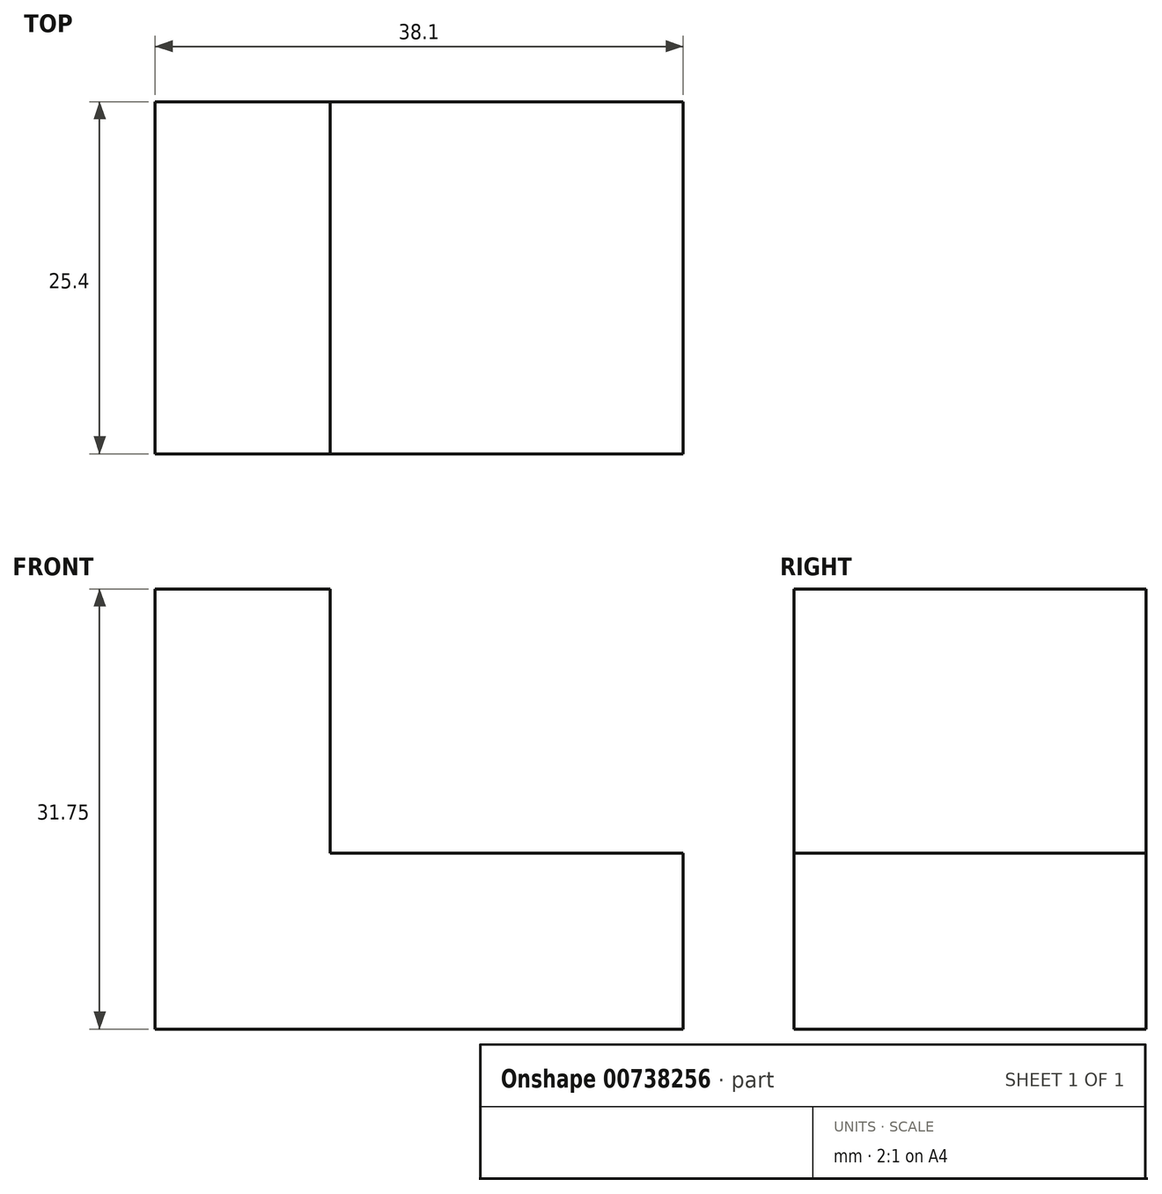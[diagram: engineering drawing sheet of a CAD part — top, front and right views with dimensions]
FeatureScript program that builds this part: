
annotation { "Feature Type Name" : "Feature", "Feature Type Description" : "" }
export const myFeature = defineFeature(function(context is Context, id is Id, definition is map)
    precondition{}
    {
        {
            var Q0;
            Q0=qCreatedBy(makeId("Front.planeOp"),FACE);
            var sketch = newSketch(context, id + "F0", { "sketchPlane" : qUnion([Q0])});
            skLineSegment(sketch, "E0", {"start": v(0, 0) * mm, "end": v(38.1, 0) * mm});
            skLineSegment(sketch, "E1", {"start": v(38.1, 0) * mm, "end": v(38.1, 31.75) * mm});
            skLineSegment(sketch, "E2", {"start": v(38.1, 31.75) * mm, "end": v(0, 31.75) * mm});
            skLineSegment(sketch, "E3", {"start": v(0, 31.75) * mm, "end": v(0, 0) * mm});
            skSolve(sketch);
        }
        {
            var Q0;
            Q0 = qSketchRegion(id + "F0", true);
            extrude(context, id + "F1", {"entities" : qUnion([Q0]), "depth" : 25.4 * mm, "offsetDistance" : 25.4 * mm});
        }
        {
            var Q0;
            Q0=makeQuery(id+"F1.opExtrude","CAP_FACE",FACE,{"disambiguationData":[OSD([sQuery(id+"F0.wireOp",EDGE,"E0"),sQuery(id+"F0.wireOp",EDGE,"E1"),sQuery(id+"F0.wireOp",EDGE,"E2"),sQuery(id+"F0.wireOp",EDGE,"E3")])],"isStart":false});
            var sketch = newSketch(context, id + "F2", { "sketchPlane" : qUnion([Q0])});
            skLineSegment(sketch, "E4", {"start": v(0, 31.75) * mm, "end": v(12.63, 31.75) * mm});
            skLineSegment(sketch, "E5", {"start": v(0, 0) * mm, "end": v(12.63, 0) * mm});
            skLineSegment(sketch, "E6", {"start": v(12.63, 12.7) * mm, "end": v(38.1, 12.7) * mm});
            skLineSegment(sketch, "E7", {"start": v(12.63, 31.75) * mm, "end": v(12.63, 12.7) * mm});
            skSolve(sketch);
        }
        {
            var Q0;
            {var subQ0=sQuery(id+"F2.wireOp",EDGE,"E6");Q0=makeQuery(id+"F2.imprint","IMPRINT",FACE,{"disambiguationData":[TD([[makeQuery(id+"F2.imprint","IMPRINT",EDGE,{"derivedFrom":subQ0}),1.0]])]});}
            extrude(context, id + "F3", {"entities" : qUnion([Q0]), "operationType" : NewBodyOperationType.REMOVE, "endBound" : BoundingType.THROUGH_ALL, "oppositeDirection" : true, "depth" : 25.4 * mm, "offsetDistance" : 25.4 * mm});
        }
    });
